# Revit family: IVLB_L4U_LF_Track Spot - EDDA L
name_source: partatom
category: Lighting Fixtures
units: mm (PartAtom-declared; Revit-internal decimal feet)

## family parameters
Always vertical = No
Cut with Voids When Loaded = No
Light Source = No
Part Type = Normal
Room Calculation Point = No
Round Connector Dimension = Use Diameter
Shared = No
Work Plane-Based = No

## types (12) — shared parameters
Apparent Load = 14 VA
Assembly Code = 63.00
Calc_Coupling_Length = 55 mm  [stored 0.180446 ft]
Description = Track Spot Edda L
IfcExportAs = IfcLightFixtureType
IfcExportType = POINTSOURCE
Lamp = LED
Manufacturer = Light4U
Model = Track Spot Edda L
Track Adapter_Height = 30 mm  [stored 0.0984252 ft]
Track Adapter_Length = 228 mm  [stored 0.748031 ft]
Track Adapter_Width = 29 mm  [stored 0.0951444 ft]
Track_Spot_Diameter = 106 mm  [stored 0.347769 ft]
Track_Spot_Length = 123 mm  [stored 0.403543 ft]
Track_Spot_Position_LR = 55 mm  [stored 0.180446 ft]
Track_Spot_Position_UD = 55 mm  [stored 0.180446 ft]
Type Comments = Edda
URL = https://light4u.io
Wattage Comments = 14W
⌂ Powered by IVLibrary = www.ivlibrary.com

## per-type parameters (varying)
| type | Light Source |
| EDDA L 1600lm_930HE 12W 20deg | Lightsource L : EDDA L 1600lm_930HE 12W 20deg_LDT |
| EDDA L 1600lm_930HE 12W 30deg | Lightsource L : EDDA L 1600lm_930HE 12W 30deg_LDT |
| EDDA L 1600lm_930HE 12W 40deg | Lightsource L : EDDA L 1600lm_930HE 12W 40deg_LDT |
| EDDA L 1600lm_930HE 12W 60deg | Lightsource L : EDDA L 1600lm_930HE 12W 60deg_LDT |
| EDDA L 2350lm_930HE 18.5W 20deg | Lightsource L : EDDA L 2350lm_930HE 18.5W 20deg_LDT |
| EDDA L 2350lm_930HE 18.5W 30deg | Lightsource L : EDDA L 2350lm_930HE 18.5W 30deg_LDT |
| EDDA L 2350lm_930HE 18.5W 40deg | Lightsource L : EDDA L 2350lm_930HE 18.5W 40deg_LDT |
| EDDA L 2350lm_930HE 18.5W 60deg | Lightsource L : EDDA L 2350lm_930HE 18.5W 60deg_LDT |
| EDDA L 3050lm_930HE 24W 20deg | Lightsource L : EDDA L 3050lm_930HE 24W 20deg_LDT |
| EDDA L 3050lm_930HE 24W 30deg | Lightsource L : EDDA L 3050lm_930HE 24W 30deg_LDT |
| EDDA L 3050lm_930HE 24W 40deg | Lightsource L : EDDA L 3050lm_930HE 24W 40deg_LDT |
| EDDA L 3050lm_930HE 24W 60deg | Lightsource L : EDDA L 3050lm_930HE 24W 60deg_LDT |

note: [stored X ft] marks values corroborated as IEEE doubles in the binary element streams (Revit-internal decimal feet)

## geometry (parser evidence)
native form markers: Sweep x19
no freeform markers — native parametric forms only
